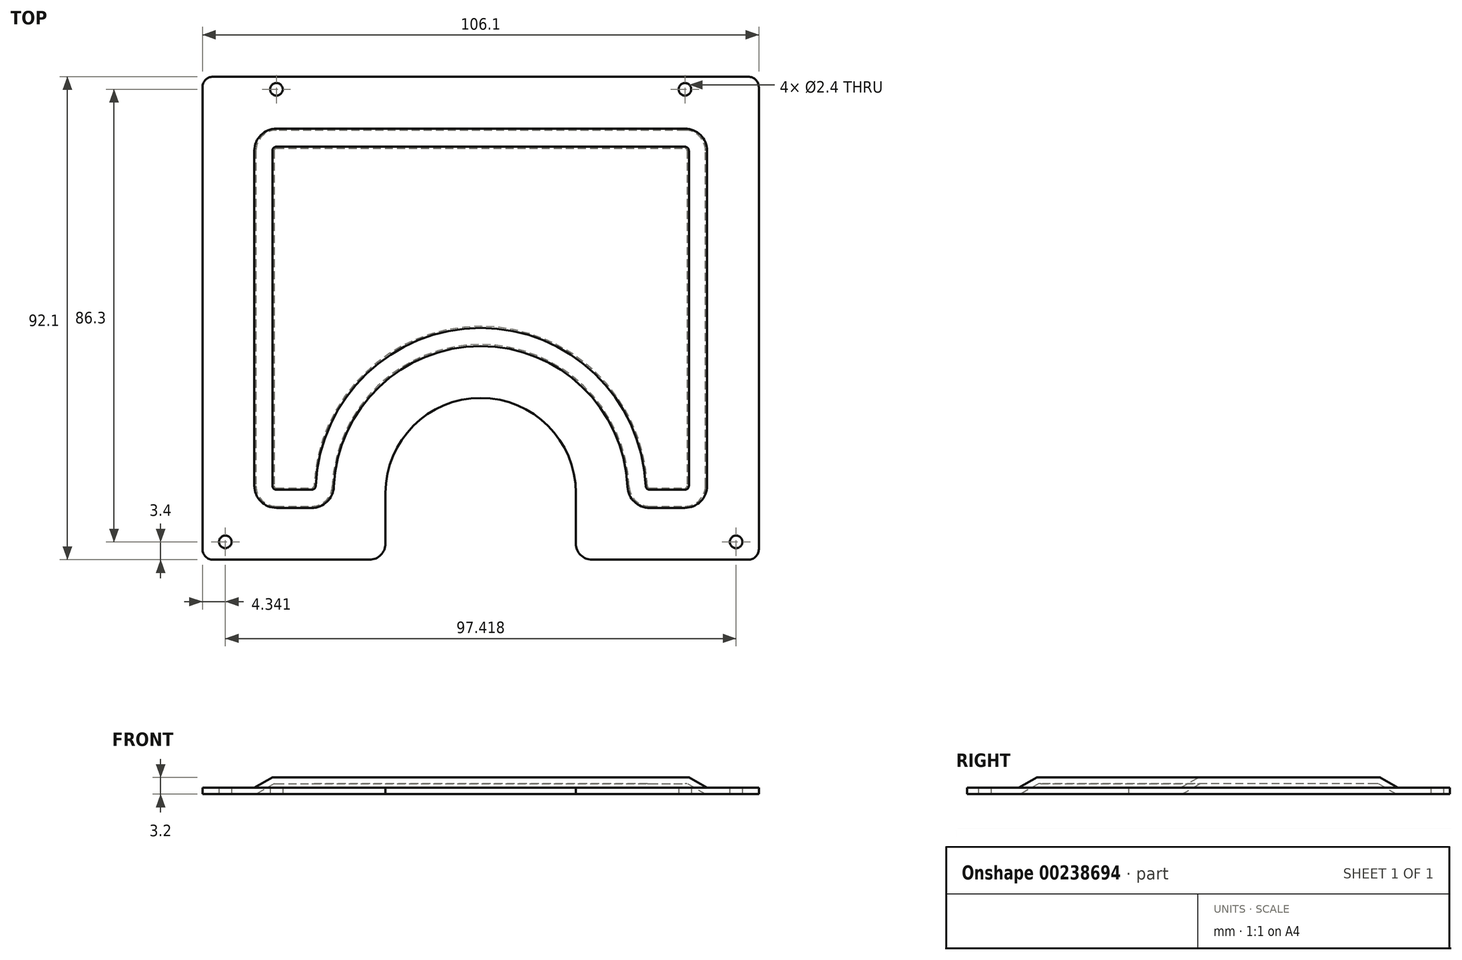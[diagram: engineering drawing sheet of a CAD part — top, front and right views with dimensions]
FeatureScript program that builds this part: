
annotation { "Feature Type Name" : "Feature", "Feature Type Description" : "" }
export const myFeature = defineFeature(function(context is Context, id is Id, definition is map)
    precondition{}
    {
        {
            var Q0;
            Q0=qCreatedBy(makeId("Top.planeOp"),FACE);
            var sketch = newSketch(context, id + "F0", { "sketchPlane" : qUnion([Q0])});
            skLineSegment(sketch, "E0.bottom", {"start": v(-51.05, 46.05) * mm, "end": v(51.05, 46.05) * mm});
            skLineSegment(sketch, "E0.top", {"start": v(-51.05, -46.05) * mm, "end": v(-21.25, -46.05) * mm});
            skLineSegment(sketch, "E0.left", {"start": v(-53.05, 44.05) * mm, "end": v(-53.05, -44.05) * mm});
            skLineSegment(sketch, "E0.right", {"start": v(53.05, 44.05) * mm, "end": v(53.05, -44.05) * mm});
            skPoint(sketch, "E1.visualSharp", {"position": v(-53.05, 46.05) * mm});
            skArc(sketch, "E1.filletArc", {"start": v(-51.05, 46.05) * mm, "mid": v(-52.46, 45.46) * mm, "end": v(-53.05, 44.05) * mm});
            skPoint(sketch, "E2.visualSharp", {"position": v(53.05, 46.05) * mm});
            skArc(sketch, "E2.filletArc", {"start": v(53.05, 44.05) * mm, "mid": v(52.46, 45.46) * mm, "end": v(51.05, 46.05) * mm});
            skPoint(sketch, "E3.visualSharp", {"position": v(53.05, -46.05) * mm});
            skArc(sketch, "E3.filletArc", {"start": v(51.05, -46.05) * mm, "mid": v(52.46, -45.46) * mm, "end": v(53.05, -44.05) * mm});
            skPoint(sketch, "E4.visualSharp", {"position": v(-53.05, -46.05) * mm});
            skArc(sketch, "E4.filletArc", {"start": v(-53.05, -44.05) * mm, "mid": v(-52.46, -45.46) * mm, "end": v(-51.05, -46.05) * mm});
            skArc(sketch, "E5", {"start": v(-18.15, -33.35) * mm, "mid": v(0, -15.2) * mm, "end": v(18.15, -33.35) * mm});
            skLineSegment(sketch, "E6", {"start": v(-18.15, -33.35) * mm, "end": v(-18.15, -42.95) * mm});
            skLineSegment(sketch, "E7", {"start": v(18.15, -33.35) * mm, "end": v(18.15, -42.95) * mm});
            skArc(sketch, "E8", {"start": v(-18.15, -42.95) * mm, "mid": v(-19.06, -45.14) * mm, "end": v(-21.25, -46.05) * mm});
            skArc(sketch, "E9", {"start": v(18.15, -42.95) * mm, "mid": v(19.06, -45.14) * mm, "end": v(21.25, -46.05) * mm});
            skLineSegment(sketch, "E10.trimOffspring", {"start": v(21.25, -46.05) * mm, "end": v(51.05, -46.05) * mm});
            skCircle(sketch, "E11", {"center": v(-38.95, 43.65) * mm, "radius": 1.2 * mm});
            skCircle(sketch, "E12", {"center": v(-48.7, -42.65) * mm, "radius": 1.2 * mm});
            skCircle(sketch, "E13.MirrorC", {"center": v(48.7, -42.65) * mm, "radius": 1.2 * mm});
            skCircle(sketch, "E14.MirrorC", {"center": v(38.95, 43.65) * mm, "radius": 1.2 * mm});
            skSolve(sketch);
        }
        {
            var Q0;
            Q0=makeQuery(id+"F0.imprint","IMPRINT",FACE,{"disambiguationData":[TD([[makeQuery(id+"F0.imprint","IMPRINT",EDGE,{"derivedFrom":sQuery(id+"F0.wireOp",EDGE,"E0.bottom")}),-1.0]])]});
            extrude(context, id + "F1", {"entities" : qUnion([Q0]), "depth" : 1.2 * mm});
        }
        {
            var Q0;
            Q0=qCreatedBy(makeId("Top.planeOp"),FACE);
            var sketch = newSketch(context, id + "F2", { "sketchPlane" : qUnion([Q0])});
            skLineSegment(sketch, "E15.0", {"start": v(-38.95, 38.25) * mm, "end": v(38.95, 38.25) * mm});
            skLineSegment(sketch, "E15.1", {"start": v(45.25, 31.95) * mm, "end": v(45.25, -31.95) * mm});
            skLineSegment(sketch, "E15.2", {"start": v(-45.25, 31.95) * mm, "end": v(-45.25, -31.95) * mm});
            skLineSegment(sketch, "E15.3", {"start": v(32.22, -38.25) * mm, "end": v(38.95, -38.25) * mm});
            skLineSegment(sketch, "E15.4", {"start": v(-38.95, -38.25) * mm, "end": v(-32.22, -38.25) * mm});
            skArc(sketch, "E15.6", {"start": v(-25.93, -32.22) * mm, "mid": v(0, -7.4) * mm, "end": v(25.93, -32.22) * mm});
            skPoint(sketch, "E16.visualSharp", {"position": v(-45.25, 38.25) * mm});
            skArc(sketch, "E16.filletArc", {"start": v(-38.95, 38.25) * mm, "mid": v(-43.4, 36.4) * mm, "end": v(-45.25, 31.95) * mm});
            skPoint(sketch, "E17.visualSharp", {"position": v(45.25, 38.25) * mm});
            skArc(sketch, "E17.filletArc", {"start": v(45.25, 31.95) * mm, "mid": v(43.4, 36.4) * mm, "end": v(38.95, 38.25) * mm});
            skPoint(sketch, "E18.visualSharp", {"position": v(45.25, -38.25) * mm});
            skArc(sketch, "E18.filletArc", {"start": v(38.95, -38.25) * mm, "mid": v(43.4, -36.4) * mm, "end": v(45.25, -31.95) * mm});
            skPoint(sketch, "E19.visualSharp", {"position": v(-45.25, -38.25) * mm});
            skArc(sketch, "E19.filletArc", {"start": v(-45.25, -31.95) * mm, "mid": v(-43.4, -36.4) * mm, "end": v(-38.95, -38.25) * mm});
            skPoint(sketch, "E20.visualSharp", {"position": v(-27.8, -38.25) * mm});
            skArc(sketch, "E20.filletArc", {"start": v(-32.22, -38.25) * mm, "mid": v(-27.86, -36.5) * mm, "end": v(-25.93, -32.22) * mm});
            skPoint(sketch, "E21.visualSharp", {"position": v(27.8, -38.25) * mm});
            skArc(sketch, "E21.filletArc", {"start": v(25.93, -32.22) * mm, "mid": v(27.86, -36.5) * mm, "end": v(32.22, -38.25) * mm});
            skSolve(sketch);
        }
        {
            var Q0;
            Q0=makeQuery(id+"F2.imprint","IMPRINT",FACE,{"disambiguationData":[TD([[makeQuery(id+"F2.imprint","IMPRINT",EDGE,{"derivedFrom":sQuery(id+"F2.wireOp",EDGE,"E15.0")}),-1.0]])]});
            extrude(context, id + "F3", {"entities" : qUnion([Q0]), "depth" : 3.2 * mm});
        }
        {
            var Q0;
            Q0=makeQuery(id+"F3.opExtrude","CAP_EDGE",EDGE,{"disambiguationData":[OSD([sQuery(id+"F2.wireOp",EDGE,"E15.2")])],"isStart":false});
            var Q1;
            Q1=makeQuery(id+"F3.opExtrude","CAP_EDGE",EDGE,{"disambiguationData":[OSD([sQuery(id+"F2.wireOp",EDGE,"E16.filletArc")])],"isStart":false});
            var Q2;
            Q2=makeQuery(id+"F3.opExtrude","CAP_EDGE",EDGE,{"disambiguationData":[OSD([sQuery(id+"F2.wireOp",EDGE,"E15.0")])],"isStart":false});
            var Q3;
            Q3=makeQuery(id+"F3.opExtrude","CAP_EDGE",EDGE,{"disambiguationData":[OSD([sQuery(id+"F2.wireOp",EDGE,"E19.filletArc")])],"isStart":false});
            var Q4;
            Q4=makeQuery(id+"F3.opExtrude","CAP_EDGE",EDGE,{"disambiguationData":[OSD([sQuery(id+"F2.wireOp",EDGE,"E15.4")])],"isStart":false});
            var Q5;
            Q5=makeQuery(id+"F3.opExtrude","CAP_EDGE",EDGE,{"disambiguationData":[OSD([sQuery(id+"F2.wireOp",EDGE,"E15.5")])],"isStart":false});
            var Q6;
            Q6=makeQuery(id+"F3.opExtrude","CAP_EDGE",EDGE,{"disambiguationData":[OSD([sQuery(id+"F2.wireOp",EDGE,"E15.6")])],"isStart":false});
            var Q7;
            Q7=makeQuery(id+"F3.opExtrude","CAP_EDGE",EDGE,{"disambiguationData":[OSD([sQuery(id+"F2.wireOp",EDGE,"E15.7")])],"isStart":false});
            var Q8;
            Q8=makeQuery(id+"F3.opExtrude","CAP_EDGE",EDGE,{"disambiguationData":[OSD([sQuery(id+"F2.wireOp",EDGE,"E15.3")])],"isStart":false});
            var Q9;
            Q9=makeQuery(id+"F3.opExtrude","CAP_EDGE",EDGE,{"disambiguationData":[OSD([sQuery(id+"F2.wireOp",EDGE,"E18.filletArc")])],"isStart":false});
            var Q10;
            Q10=makeQuery(id+"F3.opExtrude","CAP_EDGE",EDGE,{"disambiguationData":[OSD([sQuery(id+"F2.wireOp",EDGE,"E15.1")])],"isStart":false});
            var Q11;
            Q11=makeQuery(id+"F3.opExtrude","CAP_EDGE",EDGE,{"disambiguationData":[OSD([sQuery(id+"F2.wireOp",EDGE,"E17.filletArc")])],"isStart":false});
            chamfer(context, id + "F4", {"entities" : qUnion([Q0, Q1, Q2, Q3, Q4, Q5, Q6, Q7, Q8, Q9, Q10, Q11]), "chamferType" : ChamferType.OFFSET_ANGLE, "width" : 3.2 * mm, "oppositeDirection" : true, "angle" : 60 * degree, "tangentPropagation" : true});
        }
        {
            var Q0;
            Q0=makeQuery(id+"F3.opExtrude","SWEPT_BODY",BODY,{"disambiguationData":[OSD([sQuery(id+"F2.wireOp",EDGE,"E15.0"),sQuery(id+"F2.wireOp",EDGE,"E15.1"),sQuery(id+"F2.wireOp",EDGE,"E15.2"),sQuery(id+"F2.wireOp",EDGE,"E15.3"),sQuery(id+"F2.wireOp",EDGE,"E15.4"),sQuery(id+"F2.wireOp",EDGE,"E15.5"),sQuery(id+"F2.wireOp",EDGE,"E15.6"),sQuery(id+"F2.wireOp",EDGE,"E15.7"),sQuery(id+"F2.wireOp",EDGE,"E16.filletArc"),sQuery(id+"F2.wireOp",EDGE,"E17.filletArc"),sQuery(id+"F2.wireOp",EDGE,"E18.filletArc"),sQuery(id+"F2.wireOp",EDGE,"E19.filletArc")])]});
            var Q1;
            Q1=makeQuery(id+"F1.opExtrude","SWEPT_BODY",BODY,{"disambiguationData":[OSD([sQuery(id+"F0.wireOp",EDGE,"E0.bottom"),sQuery(id+"F0.wireOp",EDGE,"E0.top"),sQuery(id+"F0.wireOp",EDGE,"E0.left"),sQuery(id+"F0.wireOp",EDGE,"E0.right"),sQuery(id+"F0.wireOp",EDGE,"E1.filletArc"),sQuery(id+"F0.wireOp",EDGE,"E2.filletArc"),sQuery(id+"F0.wireOp",EDGE,"E3.filletArc"),sQuery(id+"F0.wireOp",EDGE,"E4.filletArc"),sQuery(id+"F0.wireOp",EDGE,"E5"),sQuery(id+"F0.wireOp",EDGE,"E6"),sQuery(id+"F0.wireOp",EDGE,"E7"),sQuery(id+"F0.wireOp",EDGE,"E8"),sQuery(id+"F0.wireOp",EDGE,"E9"),sQuery(id+"F0.wireOp",EDGE,"E10.trimOffspring"),sQuery(id+"F0.wireOp",EDGE,"E11"),sQuery(id+"F0.wireOp",EDGE,"E12"),sQuery(id+"F0.wireOp",EDGE,"E13.MirrorC"),sQuery(id+"F0.wireOp",EDGE,"E14.MirrorC")])]});
            booleanBodies(context, id + "F5", {"operationType" : BooleanOperationType.SUBTRACTION, "tools" : qUnion([Q0]), "targets" : qUnion([Q1]), "keepTools" : true});
        }
        {
            var Q0;
            Q0=makeQuery(id+"F3.opExtrude","CAP_FACE",FACE,{"disambiguationData":[OSD([sQuery(id+"F2.wireOp",EDGE,"E15.0"),sQuery(id+"F2.wireOp",EDGE,"E15.1"),sQuery(id+"F2.wireOp",EDGE,"E15.2"),sQuery(id+"F2.wireOp",EDGE,"E15.3"),sQuery(id+"F2.wireOp",EDGE,"E15.4"),sQuery(id+"F2.wireOp",EDGE,"E15.5"),sQuery(id+"F2.wireOp",EDGE,"E15.6"),sQuery(id+"F2.wireOp",EDGE,"E15.7"),sQuery(id+"F2.wireOp",EDGE,"E16.filletArc"),sQuery(id+"F2.wireOp",EDGE,"E17.filletArc"),sQuery(id+"F2.wireOp",EDGE,"E18.filletArc"),sQuery(id+"F2.wireOp",EDGE,"E19.filletArc")])],"isStart":true});
            shell(context, id + "F6", {"entities" : qUnion([Q0]), "thickness" : 1.2 * mm});
        }
        {
            var Q0;
            Q0=makeQuery(id+"F1.opExtrude","SWEPT_BODY",BODY,{"disambiguationData":[OSD([sQuery(id+"F0.wireOp",EDGE,"E0.bottom"),sQuery(id+"F0.wireOp",EDGE,"E0.top"),sQuery(id+"F0.wireOp",EDGE,"E0.left"),sQuery(id+"F0.wireOp",EDGE,"E0.right"),sQuery(id+"F0.wireOp",EDGE,"E1.filletArc"),sQuery(id+"F0.wireOp",EDGE,"E2.filletArc"),sQuery(id+"F0.wireOp",EDGE,"E3.filletArc"),sQuery(id+"F0.wireOp",EDGE,"E4.filletArc"),sQuery(id+"F0.wireOp",EDGE,"E5"),sQuery(id+"F0.wireOp",EDGE,"E6"),sQuery(id+"F0.wireOp",EDGE,"E7"),sQuery(id+"F0.wireOp",EDGE,"E8"),sQuery(id+"F0.wireOp",EDGE,"E9"),sQuery(id+"F0.wireOp",EDGE,"E10.trimOffspring"),sQuery(id+"F0.wireOp",EDGE,"E11"),sQuery(id+"F0.wireOp",EDGE,"E12"),sQuery(id+"F0.wireOp",EDGE,"E13.MirrorC"),sQuery(id+"F0.wireOp",EDGE,"E14.MirrorC")])]});
            var Q1;
            Q1=makeQuery(id+"F3.opExtrude","SWEPT_BODY",BODY,{"disambiguationData":[OSD([sQuery(id+"F2.wireOp",EDGE,"E15.0"),sQuery(id+"F2.wireOp",EDGE,"E15.1"),sQuery(id+"F2.wireOp",EDGE,"E15.2"),sQuery(id+"F2.wireOp",EDGE,"E15.3"),sQuery(id+"F2.wireOp",EDGE,"E15.4"),sQuery(id+"F2.wireOp",EDGE,"E15.5"),sQuery(id+"F2.wireOp",EDGE,"E15.6"),sQuery(id+"F2.wireOp",EDGE,"E15.7"),sQuery(id+"F2.wireOp",EDGE,"E16.filletArc"),sQuery(id+"F2.wireOp",EDGE,"E17.filletArc"),sQuery(id+"F2.wireOp",EDGE,"E18.filletArc"),sQuery(id+"F2.wireOp",EDGE,"E19.filletArc")])]});
            booleanBodies(context, id + "F7", {"operationType" : BooleanOperationType.UNION, "tools" : qUnion([Q0, Q1])});
        }
    });
